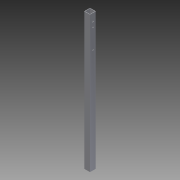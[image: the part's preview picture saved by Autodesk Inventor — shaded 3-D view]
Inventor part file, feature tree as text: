
AUTODESK INVENTOR PART (.ipt)
format: ipt  version: 2013 (Build 170138000, 138)  size: 92,160 bytes
history: native  units: in
note: dims shown in document units (in); Inventor stores cm internally (conversion verified against a paired STEP export)
features: extrude x3, sketch x3
ambient origin geometry x8: Origin, YZ Plane, XZ Plane, XY Plane, X Axis, Y Axis, Z Axis, Center Point
bodies: Solid1 (feature_tree)
feature tree (6):
  extrude  "Extrusion1"  Depth=1.0in
  extrude  "Extrusion6"  Depth=23.5in TaperAngle=0.0deg
  extrude  "Extrusion7"  Depth=1.0in TaperAngle=0.0deg
  sketch  "Sketch1"  dims[d0=1.0in d2=1.0in]
  sketch  "Sketch7"  dims[d3=0.0625in d4=23.5in d5=0.0in]
  sketch  "Sketch8"  dims[d18=1.0in d19=0.0in d20=1.0in d21=0.0in]
